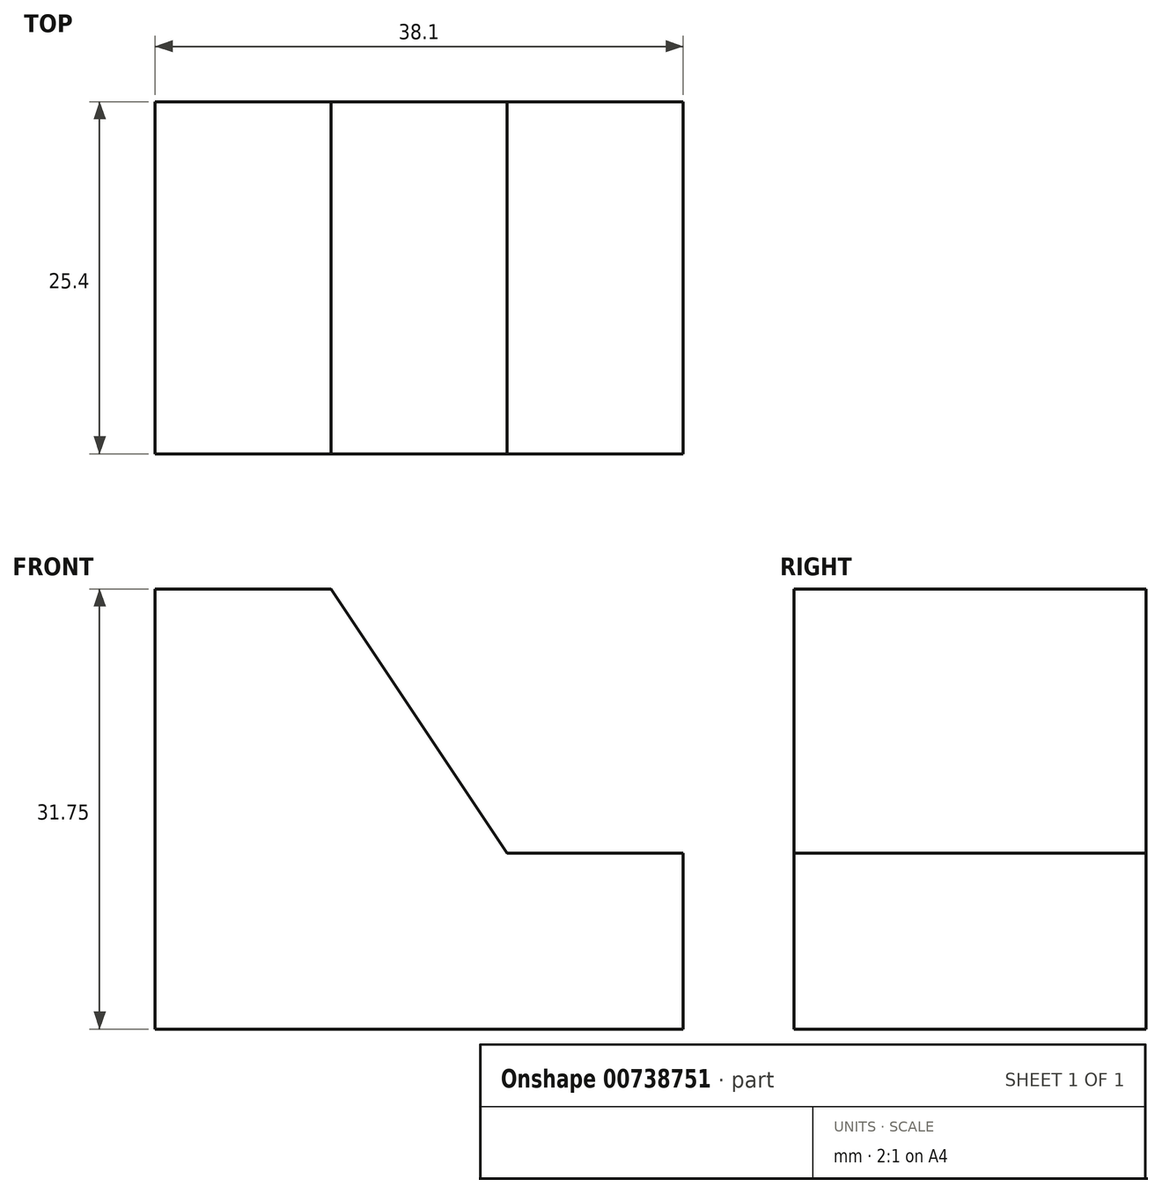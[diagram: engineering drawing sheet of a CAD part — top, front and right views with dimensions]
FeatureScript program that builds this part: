
annotation { "Feature Type Name" : "Feature", "Feature Type Description" : "" }
export const myFeature = defineFeature(function(context is Context, id is Id, definition is map)
    precondition{}
    {
        {
            var Q0;
            Q0=qCreatedBy(makeId("Front.planeOp"),FACE);
            var sketch = newSketch(context, id + "F0", { "sketchPlane" : qUnion([Q0])});
            skLineSegment(sketch, "E0", {"start": v(0, 0) * mm, "end": v(38.1, 0) * mm});
            skLineSegment(sketch, "E1", {"start": v(38.1, 0) * mm, "end": v(38.1, 31.75) * mm});
            skLineSegment(sketch, "E2", {"start": v(38.1, 31.75) * mm, "end": v(0, 31.75) * mm});
            skLineSegment(sketch, "E3", {"start": v(0, 31.75) * mm, "end": v(0, 0) * mm});
            skSolve(sketch);
        }
        {
            var Q0;
            Q0 = qSketchRegion(id + "F0", true);
            extrude(context, id + "F1", {"entities" : qUnion([Q0]), "depth" : 25.4 * mm, "offsetDistance" : 25.4 * mm});
        }
        {
            var Q0;
            Q0=makeQuery(id+"F1.opExtrude","CAP_FACE",FACE,{"disambiguationData":[OSD([sQuery(id+"F0.wireOp",EDGE,"E0"),sQuery(id+"F0.wireOp",EDGE,"E1"),sQuery(id+"F0.wireOp",EDGE,"E2"),sQuery(id+"F0.wireOp",EDGE,"E3")])],"isStart":false});
            var sketch = newSketch(context, id + "F2", { "sketchPlane" : qUnion([Q0])});
            skLineSegment(sketch, "E4", {"start": v(12.7, 31.75) * mm, "end": v(25.4, 12.7) * mm});
            skLineSegment(sketch, "E5", {"start": v(25.4, 12.7) * mm, "end": v(38.1, 12.7) * mm});
            skSolve(sketch);
        }
        {
            var Q0;
            {var subQ0=sQuery(id+"F2.wireOp",EDGE,"E4");Q0=makeQuery(id+"F2.imprint","IMPRINT",FACE,{"disambiguationData":[TD([[makeQuery(id+"F2.imprint","IMPRINT",EDGE,{"derivedFrom":subQ0}),1.0]])]});}
            extrude(context, id + "F3", {"entities" : qUnion([Q0]), "operationType" : NewBodyOperationType.REMOVE, "endBound" : BoundingType.THROUGH_ALL, "oppositeDirection" : true, "depth" : 25.4 * mm, "offsetDistance" : 25.4 * mm});
        }
    });
